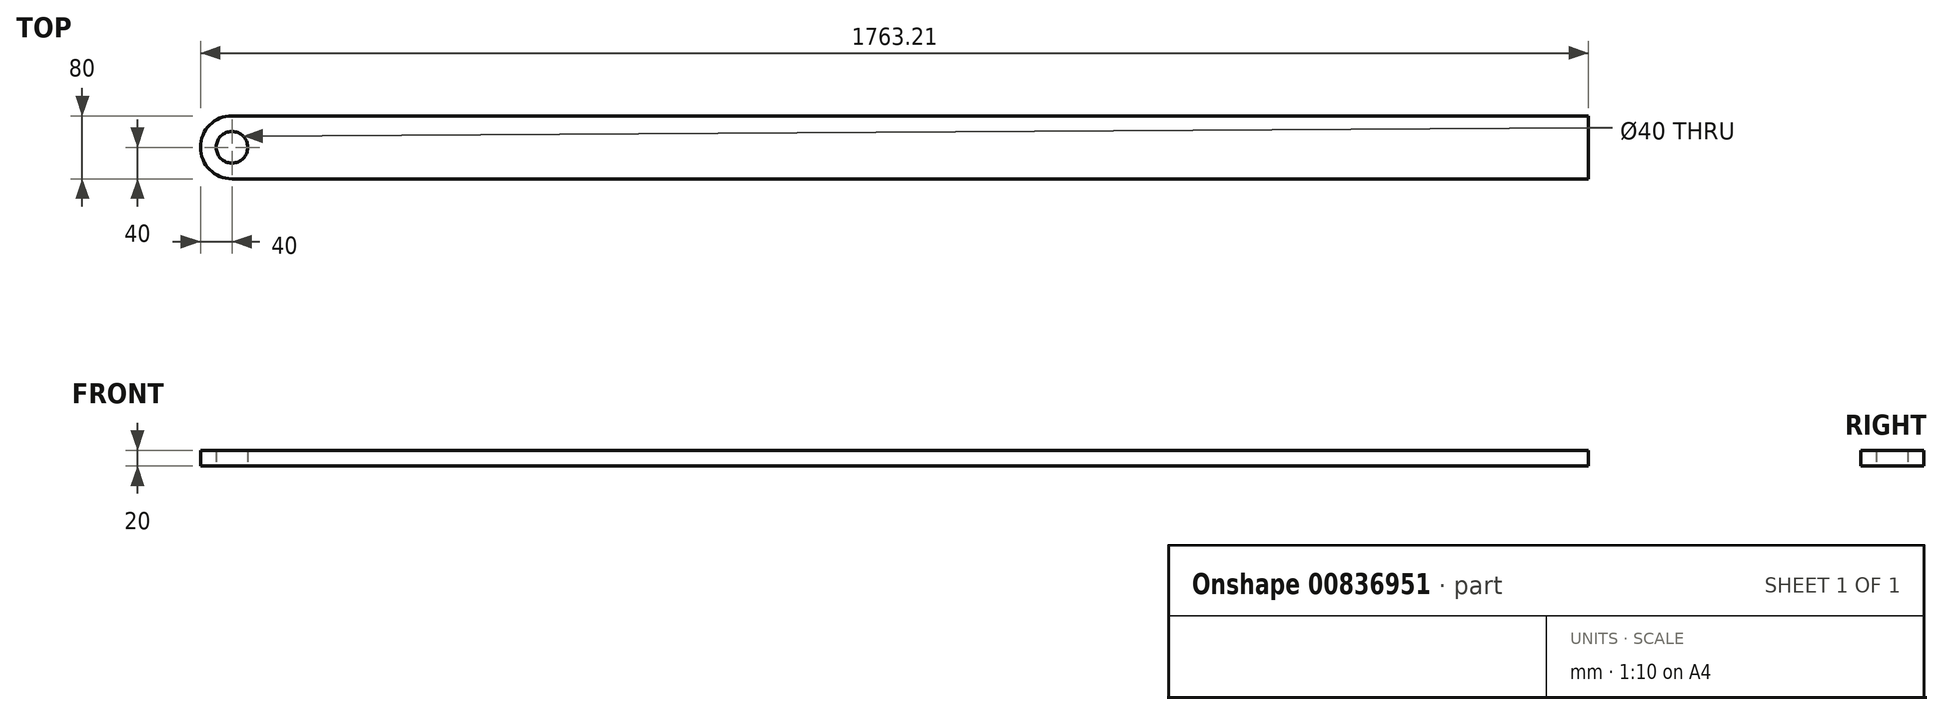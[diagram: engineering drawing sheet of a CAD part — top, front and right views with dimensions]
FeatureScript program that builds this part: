
annotation { "Feature Type Name" : "Feature", "Feature Type Description" : "" }
export const myFeature = defineFeature(function(context is Context, id is Id, definition is map)
    precondition{}
    {
        {
            var Q0;
            Q0=qCreatedBy(makeId("Top.planeOp"),FACE);
            var sketch = newSketch(context, id + "F0", { "sketchPlane" : qUnion([Q0])});
            skCircle(sketch, "E0", {"center": v(0, 0) * mm, "radius": 20 * mm});
            skLineSegment(sketch, "E1", {"start": v(0, 0) * mm, "end": v(3446.4, 0) * mm});
            skLineSegment(sketch, "E2", {"start": v(1723.2, 0) * mm, "end": v(1723.2, 414.02) * mm});
            skLineSegment(sketch, "E3", {"start": v(1723.2, 0) * mm, "end": v(1723.2, -40) * mm});
            skLineSegment(sketch, "E4", {"start": v(1723.2, -40) * mm, "end": v(0, -40) * mm});
            skLineSegment(sketch, "E5.MirrorCS", {"start": v(1723.2, 40) * mm, "end": v(0, 40) * mm});
            skArc(sketch, "E6", {"start": v(0, 40) * mm, "mid": v(-40, 0) * mm, "end": v(0, -40) * mm});
            skArc(sketch, "E7.MirrorCS", {"start": v(3446.4, 40) * mm, "mid": v(3486.4, 0) * mm, "end": v(3446.4, -40) * mm});
            skCircle(sketch, "E8.MirrorC", {"center": v(3446.4, 0) * mm, "radius": 20 * mm});
            skLineSegment(sketch, "E9.MirrorCS", {"start": v(1723.2, 40) * mm, "end": v(3446.4, 40) * mm});
            skLineSegment(sketch, "E10.MirrorCS", {"start": v(1723.2, -40) * mm, "end": v(3446.4, -40) * mm});
            skSolve(sketch);
        }
        {
            var Q0;
            Q0=makeQuery(id+"F0.imprint","IMPRINT",FACE,{"disambiguationData":[TD([[makeQuery(id+"F0.imprint","IMPRINT",EDGE,{"derivedFrom":sQuery(id+"F0.wireOp",EDGE,"E0")}),-1.0]])]});
            var Q1;
            Q1=makeQuery(id+"F0.imprint","IMPRINT",FACE,{"disambiguationData":[TD([[makeQuery(id+"F0.imprint","IMPRINT",EDGE,{"derivedFrom":sQuery(id+"F0.wireOp",EDGE,"E7.MirrorCS")}),-1.0]])]});
            extrude(context, id + "F1", {"entities" : qUnion([Q0, Q1]), "endBound" : BoundingType.SYMMETRIC, "depth" : 20 * mm, "offsetDistance" : 25 * mm});
        }
    });
